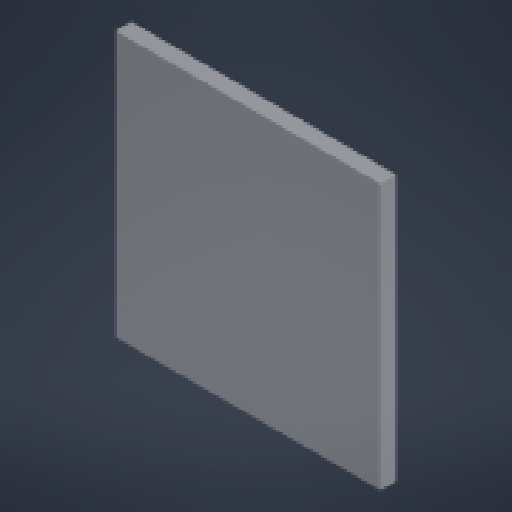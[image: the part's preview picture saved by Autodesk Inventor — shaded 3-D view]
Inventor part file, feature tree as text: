
AUTODESK INVENTOR PART (.ipt)
format: ipt  version: 2024 (Build 280153000, 153)  size: 125,440 bytes
history: native  units: mm
features: other x4, extrude x1, sketch x1, reference x1
ambient origin geometry x8: Origin, YZ Plane, XZ Plane, XY Plane, X Axis, Y Axis, Z Axis, Center Point
bodies: Body1 (feature_tree)
feature tree (7):
  other  "솔리드1"
  extrude  "돌출1"  Depth=1.5mm TaperAngle=0.0deg
  sketch  "스케치1"
  reference  "참조1"
  other  "<userpath>\Downloads\AAST\PART\AAST Remote Controler\AASTRC case.iam"
  other  "AASTRC case.iam"
  other  "AASTRC Bottom case:1"
